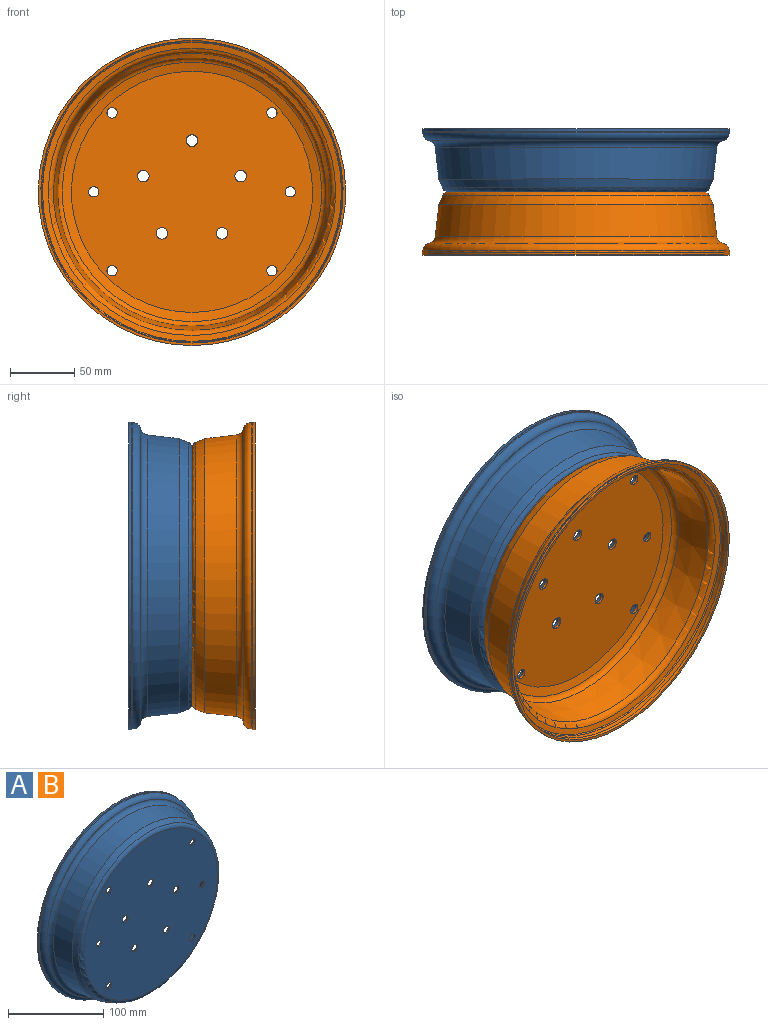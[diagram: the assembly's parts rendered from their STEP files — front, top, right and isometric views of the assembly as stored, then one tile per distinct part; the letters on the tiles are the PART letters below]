
ASSEMBLY  parts=2 mates=1
PART A: 31 faces, bbox 257.6x50.2x257.6 mm
  f0: plane 187.44x187.44mm, normal (0,1,0), area 26972.8mm2, adj f12,f20,f21,f22,f23,f24,f25,f26
  f1: plane 198.34x198.34mm, normal (0,-1,0), area 30276.2mm2, adj f18,f20,f21,f22,f23,f24,f25,f26
  f2: cone r=108.18mm half-angle=6.6deg, axis (0,1,0), area 19340.2mm2, adj f16,f19
  f3: cone r=117mm half-angle=77.5deg, axis (0,1,0), area 3348.5mm2, adj f16,f17
  f4: cylinder r=117mm len=234mm, axis (0,-1,0), area 2641.7mm2, adj f5,f17
  f5: cone r=117mm half-angle=14deg, axis (0,1,0), area 1518.8mm2, adj f4,f6
  f6: plane 239x239mm, normal (0,1,0), area 1489.1mm2, adj f5,f7
  f7: cylinder r=119.5mm len=239mm, axis (0,-1,0), area 1501.7mm2, adj f6,f8
  f8: plane 239x239mm, normal (0,-1,0), area 374.6mm2, adj f7,f9
  f9: cylinder r=119mm len=238mm, axis (0,-1,0), area 839.5mm2, adj f8,f14
  f10: cone r=119mm half-angle=77.5deg, axis (0,1,0), area 10.3mm2, adj f14,f15
  f11: cone r=110mm half-angle=6.6deg, axis (0,1,0), area 16929.4mm2, adj f13,f15
  f12: cone r=104.06mm half-angle=73.9deg, axis (0,1,0), area 4544mm2, adj f0,f19
  f13: cone r=102.5mm half-angle=22.7deg, axis (0,1,0), area 4914.2mm2, adj f11,f18
  f14: torus R=112.92mm, axis (0,1,0), area 6059.5mm2, adj f9,f10
  f15: torus R=115.54mm, axis (0,-1,0), area 5261.1mm2, adj f10,f11
  f16: torus R=112.74mm, axis (0,1,0), area 4246.6mm2, adj f2,f3
  f17: torus R=116mm, axis (0,-1,0), area 991.6mm2, adj f3,f4
  f18: torus R=99.17mm, axis (0,-1,0), area 3758.5mm2, adj f1,f13
  f19: torus R=99.48mm, axis (0,-1,0), area 3806.2mm2, adj f2,f12
  f20: cylinder r=4.5mm len=9mm, axis (0,-1,0), area 56.5mm2, adj f0,f1
  f21: cylinder r=4mm len=8mm, axis (0,-1,0), area 50.3mm2, adj f0,f1
  f22: cylinder r=4mm len=8mm, axis (0,-1,0), area 50.3mm2, adj f0,f1
  f23: cylinder r=4mm len=8mm, axis (0,-1,0), area 50.3mm2, adj f0,f1
  f24: cylinder r=4mm len=8mm, axis (0,-1,0), area 50.3mm2, adj f0,f1
  f25: cylinder r=4.5mm len=9mm, axis (0,-1,0), area 56.5mm2, adj f0,f1
  f26: cylinder r=4.5mm len=9mm, axis (0,-1,0), area 56.5mm2, adj f0,f1
  f27: cylinder r=4.5mm len=9mm, axis (0,-1,0), area 56.5mm2, adj f0,f1
  f28: cylinder r=4.5mm len=9mm, axis (0,-1,0), area 56.5mm2, adj f0,f1
  f29: cylinder r=4mm len=8mm, axis (0,-1,0), area 50.3mm2, adj f0,f1
  f30: cylinder r=4mm len=8mm, axis (0,-1,0), area 50.3mm2, adj f0,f1
PART B: same geometry as A
PLACE A t=(120.43,175.04,236.6)mm
PLACE B rot(axis=(0,0,-1),180deg) t=(120.43,175.04,236.6)mm
MATE planar A.f2 <-> B.f2  axis (0,-1,0) through (120.43,175.04,236.6)mm
